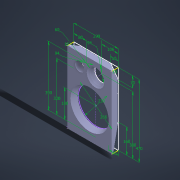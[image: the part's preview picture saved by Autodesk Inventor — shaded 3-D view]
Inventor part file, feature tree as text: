
AUTODESK INVENTOR PART (.ipt)
format: ipt  version: 2022 (Build 260153000, 153)  size: 199,680 bytes
history: native  units: mm
features: other x9, extrude x4, chamfer x3, sketch x2
ambient origin geometry x8: Origin, YZ Plane, XZ Plane, XY Plane, X Axis, Y Axis, Z Axis, Center Point
bodies: Body1 (feature_tree)
feature tree (18):
  other  "Твердое тело1"
  extrude  "Выдавливание1"  Depth=290.0mm
  sketch  "Эскиз3"
  sketch  "Эскиз4"
  chamfer  "Фаска2"  Distance=470.0mm
  chamfer  "Фаска3"  Distance=266.0mm
  other  "РабПлоскость8"
  other  "Разделение8"
  other  "РабПлоскость9"
  other  "Разделение9"
  other  "РабПлоскость10"
  other  "Разделение10"
  other  "РабПлоскость11"
  other  "Разделение11"
  chamfer  "Фаска5"  Distance=230.0mm
  extrude  "Выдавливание2"  Depth=94.0mm
  extrude  "Выдавливание3"  Depth=60.0mm
  extrude  "Выдавливание4"  Depth=94.0mm
